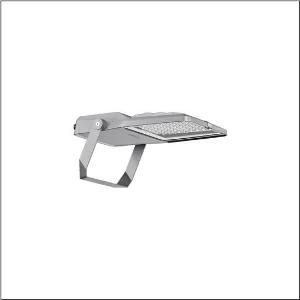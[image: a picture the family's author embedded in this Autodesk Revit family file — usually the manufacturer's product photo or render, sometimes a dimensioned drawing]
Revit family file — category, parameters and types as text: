
# Revit family: floodlight_fl_21_mini___pl43_5xa7776b2a1a_e86b
name_source: partatom
category: Lighting Fixtures
units: mm (PartAtom-declared; Revit-internal decimal feet)

## family parameters
Cut with Voids When Loaded = No
Host = Face
Light Source = No
Part Type = Normal
Room Calculation Point = No
Round Connector Dimension = Use Diameter
Shared = No

## types (1)
- --- (1 x LED, 6390 lm, 45.7 W, 3000K)
    Apparent Load = 46 VA
    CIE Flux Codes = 27 78 99 100 100
    Color Rendering = 70
    Color Temperature = 3000K
    Default Elevation = 1800 mm
    Description = Floodlight FL 21 mini, floodlight, primary light control with lens, of PMMA, primary optical cover: protective disc, of toughened safety glass, transparent, light distribution: PL43, light emission: direct distribution, installation type: surface-mounted, LED, High Power LED, rated luminous flux: 6.390lm, luminous efficacy: 140lm/W, light colour: 730, colour temperature: 3000K, control: flexible luminous flux parameterisation, time-dependent luminous flux control, constant luminous flux control, overheat protection, presetting dimming logarithmic, with terminal, 6-pole, mains connection: 220..240V, AC, 50/60Hz, start of lifetime: 46W, end of service life: 48W, reduction: 22W, luminaire housing, of diecast aluminium, powder-coated, Siteco® metallic grey (DB 702S), corrosivity category C5 mid according to DIN EN ISO 12944, sealing non-destructively replaceable, mounting bracket, of steel, galvanised, powder-coated, Siteco® metallic grey (DB 702S), Smart Interface below and above, protection rating (complete): IP66, insulation class (complete): insulation class II (safety insulation), certification: CE, ENEC, VDE, protection symbol: D, impact resistance: IK08, permissible operating ambient temperature: -40..+40°C, permissible operating ambient temperature for outdoor applications: -40..+50°C, standard: DIN EN 12944, LABS conformity tested according to VDMA 24364:2018-05, packaging unit: 1 piece

Light Distribution: PL43
    Height = 70 mm
    Lamp = 1 x LED
    Lamp Light Flux = 6390 lm
    Lamp Power = 45.7 W
    Lamp count = 1
    Length = 485 mm
    Luminous efficacy = 140 lm/W
    Manufacturer = Siteco
    ModVariant = No
    Model = 5XA7776B2A1A
    Number of Poles = 1
    OnlyDefault = Yes
    Power Factor = 1
    Product Name = Floodlight FL 21 mini | PL43
    Product group = floodlight | pylon annexe
    ProductGroupID = 6200
    Protection Class = Protection class II
    Protection Degree = IP 66
    RLX_Detail_Level = 1
    RLX_Emergency_Light_Flux = 0 lm
    RLX_Emergency_Type = 0
    RLX_Emergency_Type_DB = No
    RlxData = <blob elided: 95777 chars, md5=529fe4a9>
    Socket = socket
    Standby Power = 0 W
    System Light Flux = 6390 lm
    System Power = 46 W
    Type Comments = factory setting: luminous flux: 100 % | dim-lin: 254 | 463 mA
    Type Image = l_1006845.jpg
    URL = http://relux.com
    VarID = @adj_093591
    Voltage = 0 V
    Weight = 0.00 kg
    Width = 337 mm

## geometry (parser evidence)
native form markers: Blend x4, Sweep x12
no freeform markers — native parametric forms only
